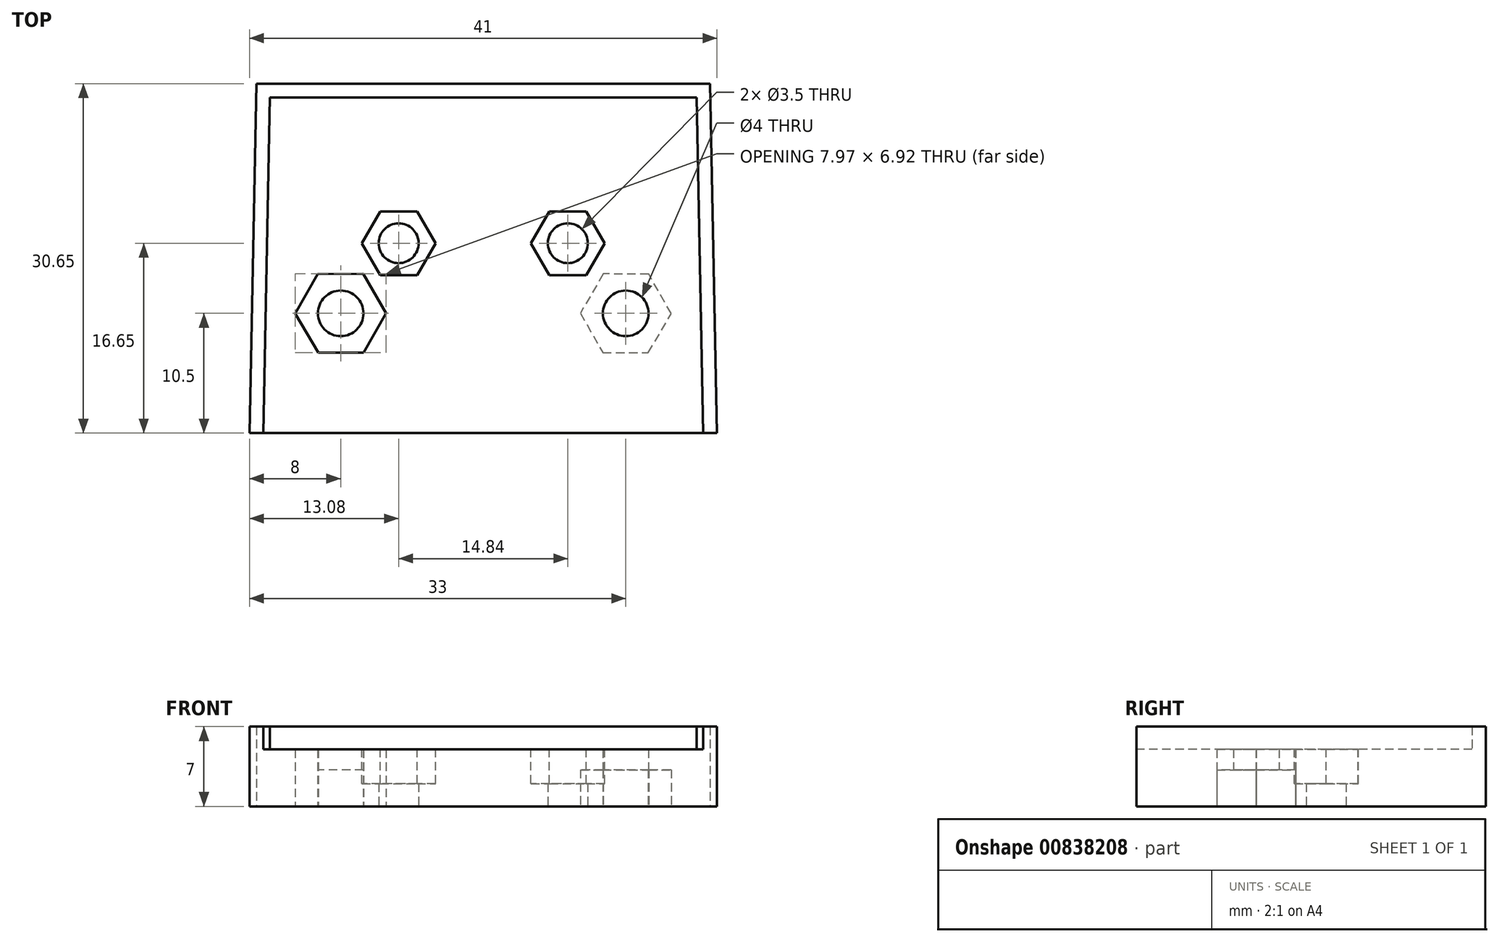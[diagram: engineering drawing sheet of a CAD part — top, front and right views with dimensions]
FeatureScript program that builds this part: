
annotation { "Feature Type Name" : "Feature", "Feature Type Description" : "" }
export const myFeature = defineFeature(function(context is Context, id is Id, definition is map)
    precondition{}
    {
        {
            var Q0;
            Q0=qCreatedBy(makeId("Top.planeOp"),FACE);
            var sketch = newSketch(context, id + "F0", { "sketchPlane" : qUnion([Q0])});
            skLineSegment(sketch, "E0", {"start": v(-63.12, 0) * mm, "end": v(68.41, 0) * mm, "construction": true});
            skLineSegment(sketch, "E1", {"start": v(0, 49.05) * mm, "end": v(0, -54.34) * mm, "construction": true});
            skCircle(sketch, "E2", {"center": v(12.5, 0) * mm, "radius": 2 * mm});
            skCircle(sketch, "E3.MirrorC", {"center": v(-12.5, 0) * mm, "radius": 2 * mm});
            skLineSegment(sketch, "E4", {"start": v(0, 20.15) * mm, "end": v(19.9, 20.15) * mm});
            skLineSegment(sketch, "E5", {"start": v(19.9, 20.15) * mm, "end": v(20.5, -10.5) * mm});
            skLineSegment(sketch, "E6", {"start": v(20.5, -10.5) * mm, "end": v(0, -10.5) * mm});
            skLineSegment(sketch, "E7", {"start": v(-23.47, 6.15) * mm, "end": v(37.66, 6.15) * mm, "construction": true});
            skLineSegment(sketch, "E8", {"start": v(7.42, 25.27) * mm, "end": v(7.42, -3.64) * mm, "construction": true});
            skCircle(sketch, "E9", {"center": v(7.42, 6.15) * mm, "radius": 1.75 * mm});
            skLineSegment(sketch, "E10.0", {"start": v(18.72, 18.95) * mm, "end": v(19.3, -10.52) * mm});
            skLineSegment(sketch, "E10.1", {"start": v(0, 18.95) * mm, "end": v(18.72, 18.95) * mm});
            skLineSegment(sketch, "E11.MirrorCS", {"start": v(0, 20.15) * mm, "end": v(-19.9, 20.15) * mm});
            skLineSegment(sketch, "E12.MirrorCS", {"start": v(0, 18.95) * mm, "end": v(-18.72, 18.95) * mm});
            skLineSegment(sketch, "E13.MirrorCS", {"start": v(-18.72, 18.95) * mm, "end": v(-19.3, -10.52) * mm});
            skLineSegment(sketch, "E14.MirrorCS", {"start": v(-19.9, 20.15) * mm, "end": v(-20.5, -10.5) * mm});
            skLineSegment(sketch, "E15.MirrorCS", {"start": v(-20.5, -10.5) * mm, "end": v(0, -10.5) * mm});
            skCircle(sketch, "E16.MirrorC", {"center": v(-7.42, 6.15) * mm, "radius": 1.75 * mm});
            skCircle(sketch, "E17.cCircle", {"center": v(-12.5, 0) * mm, "radius": 3.45 * mm, "construction": true});
            skLineSegment(sketch, "E17.0", {"start": v(-16.48, -0.02) * mm, "end": v(-14.51, 3.44) * mm});
            skLineSegment(sketch, "E17.1", {"start": v(-14.51, 3.44) * mm, "end": v(-10.53, 3.46) * mm});
            skLineSegment(sketch, "E17.2", {"start": v(-10.53, 3.46) * mm, "end": v(-8.52, 0.02) * mm});
            skLineSegment(sketch, "E17.3", {"start": v(-8.52, 0.02) * mm, "end": v(-10.49, -3.44) * mm});
            skLineSegment(sketch, "E17.4", {"start": v(-10.49, -3.44) * mm, "end": v(-14.47, -3.46) * mm});
            skLineSegment(sketch, "E17.5", {"start": v(-14.47, -3.46) * mm, "end": v(-16.48, -0.02) * mm});
            skPoint(sketch, "E17.0.midPoint", {"position": v(-15.5, 1.7) * mm});
            skLineSegment(sketch, "E18.MirrorCS", {"start": v(16.48, -0.02) * mm, "end": v(14.51, 3.44) * mm});
            skCircle(sketch, "E19.MirrorC", {"center": v(12.5, 0) * mm, "radius": 3.45 * mm, "construction": true});
            skLineSegment(sketch, "E20.MirrorCS", {"start": v(14.47, -3.46) * mm, "end": v(16.48, -0.02) * mm});
            skLineSegment(sketch, "E21.MirrorCS", {"start": v(10.49, -3.44) * mm, "end": v(14.47, -3.46) * mm});
            skLineSegment(sketch, "E22.MirrorCS", {"start": v(14.51, 3.44) * mm, "end": v(10.53, 3.46) * mm});
            skPoint(sketch, "E23.MirrorP", {"position": v(15.5, 1.7) * mm});
            skLineSegment(sketch, "E24.MirrorCS", {"start": v(10.53, 3.46) * mm, "end": v(8.52, 0.02) * mm});
            skLineSegment(sketch, "E25.MirrorCS", {"start": v(8.52, 0.02) * mm, "end": v(10.49, -3.44) * mm});
            skSolve(sketch);
        }
        {
            var Q0;
            Q0=makeQuery(id+"F0.imprint","IMPRINT",FACE,{"disambiguationData":[TD([[makeQuery(id+"F0.imprint","IMPRINT",EDGE,{"derivedFrom":sQuery(id+"F0.wireOp",EDGE,"E2")}),-1.0]])]});
            var Q1;
            Q1=makeQuery(id+"F0.imprint","IMPRINT",FACE,{"disambiguationData":[TD([[makeQuery(id+"F0.imprint","IMPRINT",EDGE,{"derivedFrom":sQuery(id+"F0.wireOp",EDGE,"E9")}),-1.0]])]});
            var Q2;
            Q2=makeQuery(id+"F0.imprint","IMPRINT",FACE,{"disambiguationData":[TD([[makeQuery(id+"F0.imprint","IMPRINT",EDGE,{"derivedFrom":sQuery(id+"F0.wireOp",EDGE,"E3.MirrorC")}),1.0]])]});
            var Q3;
            Q3=makeQuery(id+"F0.imprint","IMPRINT",FACE,{"disambiguationData":[TD([[makeQuery(id+"F0.imprint","IMPRINT",EDGE,{"derivedFrom":sQuery(id+"F0.wireOp",EDGE,"E18.MirrorCS")}),1.0]])]});
            extrude(context, id + "F1", {"entities" : qUnion([Q0, Q1, Q2, Q3]), "depth" : 5 * mm, "offsetDistance" : 25 * mm});
        }
        {
            var Q0;
            Q0=makeQuery(id+"F0.imprint","IMPRINT",FACE,{"disambiguationData":[TD([[makeQuery(id+"F0.imprint","IMPRINT",EDGE,{"derivedFrom":sQuery(id+"F0.wireOp",EDGE,"E4")}),-1.0]])]});
            extrude(context, id + "F2", {"entities" : qUnion([Q0]), "operationType" : NewBodyOperationType.ADD, "depth" : 7 * mm, "offsetDistance" : 25 * mm});
        }
        {
            var Q0;
            Q0=makeQuery(id+"F0.imprint","IMPRINT",FACE,{"disambiguationData":[TD([[makeQuery(id+"F0.imprint","IMPRINT",EDGE,{"derivedFrom":sQuery(id+"F0.wireOp",EDGE,"E18.MirrorCS")}),1.0]])]});
            var Q1;
            Q1=makeQuery(id+"F0.imprint","IMPRINT",FACE,{"disambiguationData":[TD([[makeQuery(id+"F0.imprint","IMPRINT",EDGE,{"derivedFrom":sQuery(id+"F0.wireOp",EDGE,"E3.MirrorC")}),1.0]])]});
            extrude(context, id + "F3", {"entities" : qUnion([Q0, Q1]), "operationType" : NewBodyOperationType.REMOVE, "depth" : 3.2 * mm, "offsetDistance" : 25 * mm});
        }
        {
            var Q0;
            Q0=makeQuery(id+"F1.opExtrude","CAP_FACE",FACE,{"disambiguationData":[OSD([sQuery(id+"F0.wireOp",EDGE,"E3.MirrorC"),sQuery(id+"F0.wireOp",EDGE,"E6"),sQuery(id+"F0.wireOp",EDGE,"E9"),sQuery(id+"F0.wireOp",EDGE,"E10.0"),sQuery(id+"F0.wireOp",EDGE,"E10.1"),sQuery(id+"F0.wireOp",EDGE,"E12.MirrorCS"),sQuery(id+"F0.wireOp",EDGE,"E13.MirrorCS"),sQuery(id+"F0.wireOp",EDGE,"E15.MirrorCS"),sQuery(id+"F0.wireOp",EDGE,"E16.MirrorC"),sQuery(id+"F0.wireOp",EDGE,"E2")])],"isStart":false});
            var sketch = newSketch(context, id + "F4", { "sketchPlane" : qUnion([Q0])});
            skLineSegment(sketch, "E26", {"start": v(-23.47, 6.15) * mm, "end": v(37.66, 6.15) * mm, "construction": true});
            skLineSegment(sketch, "E27", {"start": v(7.42, 25.27) * mm, "end": v(7.42, -3.64) * mm, "construction": true});
            skCircle(sketch, "E28.cCircle", {"center": v(7.42, 6.15) * mm, "radius": 2.8 * mm, "construction": true});
            skLineSegment(sketch, "E28.0", {"start": v(9.04, 8.95) * mm, "end": v(10.65, 6.15) * mm});
            skLineSegment(sketch, "E28.1", {"start": v(10.65, 6.15) * mm, "end": v(9.04, 3.35) * mm});
            skLineSegment(sketch, "E28.2", {"start": v(9.04, 3.35) * mm, "end": v(5.8, 3.35) * mm});
            skLineSegment(sketch, "E28.3", {"start": v(5.8, 3.35) * mm, "end": v(4.19, 6.15) * mm});
            skLineSegment(sketch, "E28.4", {"start": v(4.19, 6.15) * mm, "end": v(5.8, 8.95) * mm});
            skLineSegment(sketch, "E28.5", {"start": v(5.8, 8.95) * mm, "end": v(9.04, 8.95) * mm});
            skPoint(sketch, "E28.0.midPoint", {"position": v(9.85, 7.55) * mm});
            skCircle(sketch, "E29.MirrorC", {"center": v(-7.42, 6.15) * mm, "radius": 2.8 * mm, "construction": true});
            skLineSegment(sketch, "E30.MirrorCS", {"start": v(-5.8, 8.95) * mm, "end": v(-9.04, 8.95) * mm});
            skLineSegment(sketch, "E31.MirrorCS", {"start": v(-4.19, 6.15) * mm, "end": v(-5.8, 8.95) * mm});
            skLineSegment(sketch, "E32.MirrorCS", {"start": v(-5.8, 3.35) * mm, "end": v(-4.19, 6.15) * mm});
            skLineSegment(sketch, "E33.MirrorCS", {"start": v(-9.04, 3.35) * mm, "end": v(-5.8, 3.35) * mm});
            skLineSegment(sketch, "E34.MirrorCS", {"start": v(-10.65, 6.15) * mm, "end": v(-9.04, 3.35) * mm});
            skLineSegment(sketch, "E35.MirrorCS", {"start": v(-9.04, 8.95) * mm, "end": v(-10.65, 6.15) * mm});
            skSolve(sketch);
        }
        {
            var Q0;
            Q0 = qSketchRegion(id + "F4", true);
            extrude(context, id + "F5", {"entities" : qUnion([Q0]), "operationType" : NewBodyOperationType.REMOVE, "oppositeDirection" : true, "depth" : 3 * mm, "offsetDistance" : 25 * mm});
        }
    });
